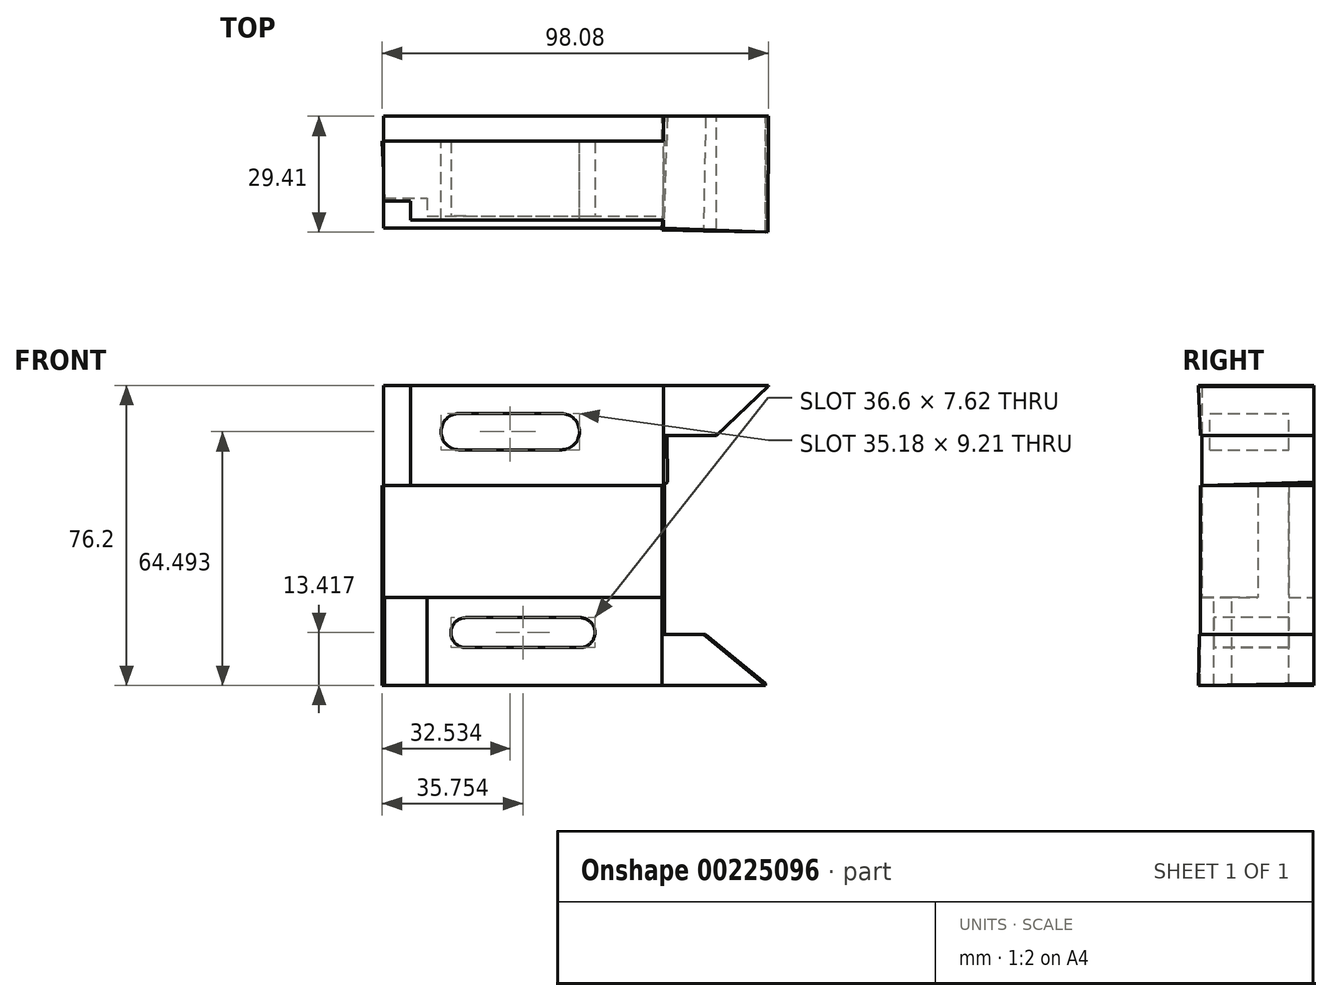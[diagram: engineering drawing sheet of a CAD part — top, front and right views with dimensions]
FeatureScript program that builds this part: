
annotation { "Feature Type Name" : "Feature", "Feature Type Description" : "" }
export const myFeature = defineFeature(function(context is Context, id is Id, definition is map)
    precondition{}
    {
        {
            var Q0;
            Q0=qCreatedBy(makeId("Front.planeOp"),FACE);
            var sketch = newSketch(context, id + "F0", { "sketchPlane" : qUnion([Q0])});
            skLineSegment(sketch, "E0.bottom", {"start": v(-31.28, 0) * mm, "end": v(39.84, 0) * mm});
            skLineSegment(sketch, "E0.top", {"start": v(-31.28, -28.45) * mm, "end": v(39.84, -28.45) * mm});
            skLineSegment(sketch, "E0.left", {"start": v(-31.28, 0) * mm, "end": v(-31.28, -28.45) * mm});
            skLineSegment(sketch, "E0.right", {"start": v(39.84, 0) * mm, "end": v(39.84, -28.45) * mm});
            skSolve(sketch);
        }
        {
            var Q0;
            Q0 = qSketchRegion(id + "F0", true);
            extrude(context, id + "F1", {"entities" : qUnion([Q0]), "depth" : 28.45 * mm});
        }
        {
            var Q0;
            Q0=makeQuery(id+"F1.opExtrude","SWEPT_FACE",FACE,{"disambiguationData":[OSD([sQuery(id+"F0.wireOp",EDGE,"E0.bottom")])]});
            var sketch = newSketch(context, id + "F2", { "sketchPlane" : qUnion([Q0])});
            skLineSegment(sketch, "E1", {"start": v(-31.28, -6.35) * mm, "end": v(39.84, -6.35) * mm});
            skLineSegment(sketch, "E2", {"start": v(39.84, -6.35) * mm, "end": v(39.84, 0) * mm});
            skLineSegment(sketch, "E3", {"start": v(39.84, 0) * mm, "end": v(39.84, 0) * mm});
            skLineSegment(sketch, "E4", {"start": v(39.84, -28.45) * mm, "end": v(39.84, -28.45) * mm});
            skLineSegment(sketch, "E5", {"start": v(39.84, -28.45) * mm, "end": v(39.84, -26.42) * mm});
            skLineSegment(sketch, "E6", {"start": v(39.84, -26.42) * mm, "end": v(-24.36, -26.42) * mm});
            skLineSegment(sketch, "E7", {"start": v(-24.36, -26.42) * mm, "end": v(-24.36, -21.59) * mm});
            skLineSegment(sketch, "E8", {"start": v(-24.36, -21.59) * mm, "end": v(-31.28, -21.59) * mm});
            skLineSegment(sketch, "E9", {"start": v(-31.28, -21.59) * mm, "end": v(-31.28, -6.35) * mm});
            skLineSegment(sketch, "E10", {"start": v(39.84, 0) * mm, "end": v(66.5, 0) * mm});
            skLineSegment(sketch, "E11", {"start": v(66.5, 0) * mm, "end": v(66.47, -29.37) * mm});
            skLineSegment(sketch, "E12", {"start": v(66.47, -29.37) * mm, "end": v(39.84, -28.45) * mm});
            skSolve(sketch);
        }
        {
            var Q0;
            {var subQ0=sQuery(id+"F2.wireOp",EDGE,"E1");Q0=makeQuery(id+"F2.imprint","IMPRINT",FACE,{"disambiguationData":[TD([[makeQuery(id+"F2.imprint","IMPRINT",EDGE,{"derivedFrom":subQ0}),-1.0]])]});}
            var Q1;
            {var subQ0=sQuery(id+"F2.wireOp",EDGE,"E2");Q1=makeQuery(id+"F2.imprint","IMPRINT",FACE,{"disambiguationData":[TD([[makeQuery(id+"F2.imprint","IMPRINT",EDGE,{"derivedFrom":subQ0}),-1.0]])]});}
            extrude(context, id + "F3", {"entities" : qUnion([Q0, Q1]), "operationType" : NewBodyOperationType.ADD, "oppositeDirection" : true, "depth" : 25.4 * mm});
        }
        {
            var Q0;
            Q0 = qSketchRegion(id + "F2", true);
            extrude(context, id + "F4", {"entities" : qUnion([Q0]), "operationType" : NewBodyOperationType.ADD, "depth" : 25.4 * mm});
        }
        {
            var Q0;
            Q0=qCreatedBy(makeId("Front.planeOp"),FACE);
            var sketch = newSketch(context, id + "F5", { "sketchPlane" : qUnion([Q0])});
            skLineSegment(sketch, "E13", {"start": v(-12.04, 18.3) * mm, "end": v(13.93, 18.3) * mm});
            skLineSegment(sketch, "E14", {"start": v(-12.04, 9.09) * mm, "end": v(13.93, 9.09) * mm});
            skArc(sketch, "E15", {"start": v(-12.04, 18.3) * mm, "mid": v(-16.64, 13.7) * mm, "end": v(-12.04, 9.09) * mm});
            skArc(sketch, "E16", {"start": v(13.93, 9.09) * mm, "mid": v(18.53, 13.7) * mm, "end": v(13.93, 18.3) * mm});
            skLineSegment(sketch, "E17", {"start": v(39.9, 0) * mm, "end": v(69.92, 0) * mm});
            skLineSegment(sketch, "E18", {"start": v(69.92, 0) * mm, "end": v(69.92, 28.45) * mm});
            skLineSegment(sketch, "E19", {"start": v(69.92, 28.45) * mm, "end": v(39.9, 0) * mm});
            skSolve(sketch);
        }
        {
            var Q0;
            Q0 = qSketchRegion(id + "F5", true);
            extrude(context, id + "F6", {"entities" : qUnion([Q0]), "operationType" : NewBodyOperationType.REMOVE, "endBound" : BoundingType.THROUGH_ALL, "depth" : 25.4 * mm});
        }
        {
            var Q0;
            {var subQ0=sQuery(id+"F2.wireOp",EDGE,"E12");Q0=makeQuery(id+"F4.boolean.opBoolean","MERGE",FACE,{"derivedFrom":[makeQuery(id+"F3.opExtrude","SWEPT_FACE",FACE,{"disambiguationData":[OSD([subQ0])]}),makeQuery(id+"F4.opExtrude","SWEPT_FACE",FACE,{"disambiguationData":[OSD([subQ0])]})]});}
            var sketch = newSketch(context, id + "F7", { "sketchPlane" : qUnion([Q0])});
            skPoint(sketch, "E20.0", {"position": v(40.8, 12.7) * mm});
            skLineSegment(sketch, "E21", {"start": v(40.8, 12.7) * mm, "end": v(54.27, 12.7) * mm});
            skLineSegment(sketch, "E22", {"start": v(54.27, 12.7) * mm, "end": v(40.85, 0) * mm});
            skLineSegment(sketch, "E23", {"start": v(40.85, 0) * mm, "end": v(40.8, 12.7) * mm});
            skSolve(sketch);
        }
        {
            var Q0;
            Q0 = qSketchRegion(id + "F7", true);
            extrude(context, id + "F8", {"entities" : qUnion([Q0]), "operationType" : NewBodyOperationType.REMOVE, "endBound" : BoundingType.THROUGH_ALL, "oppositeDirection" : true, "depth" : 25.4 * mm});
        }
        {
            var Q0;
            {var subQ2=sQuery(id+"F2.wireOp",EDGE,"E12");var subQ10=makeQuery(id+"F4.opExtrude","SWEPT_FACE",FACE,{"disambiguationData":[OSD([subQ2])]});var subQ11=sQuery(id+"F0.wireOp",EDGE,"E0.bottom");var subQ12=makeQuery(id+"F3.opExtrude","SWEPT_FACE",FACE,{"disambiguationData":[OSD([subQ2])]});Q0=makeQuery(id+"F8.boolean.opBoolean","SPLIT",FACE,{"disambiguationData":[TD([makeQuery(id+"F1.opExtrude","SWEPT_FACE",FACE,{"disambiguationData":[OSD([subQ11])]})])],"derivedFrom":makeQuery(id+"F4.boolean.opBoolean","MERGE",FACE,{"derivedFrom":[subQ12,subQ10]})});}
            var sketch = newSketch(context, id + "F9", { "sketchPlane" : qUnion([Q0])});
            skLineSegment(sketch, "E24.bottom", {"start": v(40.85, 0) * mm, "end": v(67.45, 0) * mm});
            skLineSegment(sketch, "E24.top", {"start": v(40.85, -25.4) * mm, "end": v(67.45, -25.4) * mm});
            skLineSegment(sketch, "E24.left", {"start": v(40.85, 0) * mm, "end": v(40.85, -25.4) * mm});
            skLineSegment(sketch, "E24.right", {"start": v(67.45, 0) * mm, "end": v(67.45, -25.4) * mm});
            skSolve(sketch);
        }
        {
            var Q0;
            Q0 = qSketchRegion(id + "F9", true);
            extrude(context, id + "F10", {"entities" : qUnion([Q0]), "operationType" : NewBodyOperationType.REMOVE, "endBound" : BoundingType.THROUGH_ALL, "oppositeDirection" : true, "depth" : 25.4 * mm});
        }
        {
            var Q0;
            Q0=qCreatedBy(makeId("Top.planeOp"),FACE);
            var sketch = newSketch(context, id + "F11", { "sketchPlane" : qUnion([Q0])});
            skLineSegment(sketch, "E25", {"start": v(-31.6, -6.35) * mm, "end": v(39.53, -6.35) * mm});
            skLineSegment(sketch, "E26", {"start": v(39.53, -6.35) * mm, "end": v(39.53, 0) * mm});
            skLineSegment(sketch, "E27", {"start": v(39.53, 0) * mm, "end": v(65.76, 0) * mm});
            skLineSegment(sketch, "E28", {"start": v(65.76, 0) * mm, "end": v(65.76, -29.4) * mm});
            skLineSegment(sketch, "E29", {"start": v(-31.03, -20.83) * mm, "end": v(-20.23, -20.83) * mm});
            skLineSegment(sketch, "E30", {"start": v(-20.23, -20.83) * mm, "end": v(-20.23, -25.37) * mm});
            skLineSegment(sketch, "E31", {"start": v(-20.23, -25.37) * mm, "end": v(33.45, -25.37) * mm});
            skLineSegment(sketch, "E32", {"start": v(33.45, -25.37) * mm, "end": v(39.53, -25.37) * mm});
            skLineSegment(sketch, "E33", {"start": v(39.53, -25.37) * mm, "end": v(39.53, -28.89) * mm});
            skLineSegment(sketch, "E34", {"start": v(65.76, -29.4) * mm, "end": v(39.53, -28.89) * mm});
            skLineSegment(sketch, "E35", {"start": v(-31.6, -6.35) * mm, "end": v(-31.03, -20.83) * mm});
            skSolve(sketch);
        }
        {
            var Q0;
            Q0 = qSketchRegion(id + "F11", true);
            extrude(context, id + "F12", {"entities" : qUnion([Q0]), "operationType" : NewBodyOperationType.ADD, "oppositeDirection" : true, "depth" : 50.8 * mm});
        }
        {
            var Q0;
            Q0=makeQuery(id+"F12.opExtrude","SWEPT_FACE",FACE,{"disambiguationData":[OSD([sQuery(id+"F11.wireOp",EDGE,"E31"),sQuery(id+"F11.wireOp",EDGE,"E32")])]});
            var sketch = newSketch(context, id + "F13", { "sketchPlane" : qUnion([Q0])});
            skLineSegment(sketch, "E36", {"start": v(-10.33, -33.57) * mm, "end": v(18.41, -33.57) * mm});
            skLineSegment(sketch, "E37", {"start": v(-10.33, -41.2) * mm, "end": v(18.41, -41.2) * mm});
            skArc(sketch, "E38", {"start": v(-10.33, -33.57) * mm, "mid": v(-14.14, -37.38) * mm, "end": v(-10.33, -41.2) * mm});
            skArc(sketch, "E39", {"start": v(18.41, -41.2) * mm, "mid": v(22.46, -37.38) * mm, "end": v(18.41, -33.57) * mm});
            skLineSegment(sketch, "E40", {"start": v(39.53, -28.45) * mm, "end": v(65.92, -50.14) * mm});
            skLineSegment(sketch, "E41", {"start": v(39.53, -28.45) * mm, "end": v(39.53, 0) * mm});
            skLineSegment(sketch, "E42", {"start": v(39.53, 0) * mm, "end": v(65.62, 0) * mm});
            skLineSegment(sketch, "E43", {"start": v(65.62, 0) * mm, "end": v(65.92, -50.14) * mm});
            skSolve(sketch);
        }
        {
            var Q0;
            Q0=makeQuery(id+"F13.imprint","IMPRINT",FACE,{"disambiguationData":[TD([[makeQuery(id+"F13.imprint","IMPRINT",EDGE,{"derivedFrom":sQuery(id+"F13.wireOp",EDGE,"E36")}),-1.0]])]});
            extrude(context, id + "F14", {"entities" : qUnion([Q0]), "operationType" : NewBodyOperationType.REMOVE, "endBound" : BoundingType.THROUGH_ALL, "oppositeDirection" : true, "depth" : 25.4 * mm});
        }
        {
            var Q0;
            Q0=makeQuery(id+"F12.opExtrude","SWEPT_FACE",FACE,{"disambiguationData":[OSD([sQuery(id+"F11.wireOp",EDGE,"E34")])]});
            var sketch = newSketch(context, id + "F15", { "sketchPlane" : qUnion([Q0])});
            skLineSegment(sketch, "E44", {"start": v(40.1, 0) * mm, "end": v(66.33, 0) * mm});
            skLineSegment(sketch, "E45", {"start": v(66.33, 0) * mm, "end": v(66.33, -50.8) * mm});
            skLineSegment(sketch, "E46", {"start": v(66.33, -50.8) * mm, "end": v(40.1, -29.18) * mm});
            skLineSegment(sketch, "E47", {"start": v(40.1, -29.18) * mm, "end": v(40.1, 0) * mm});
            skSolve(sketch);
        }
        {
            var Q0;
            Q0 = qSketchRegion(id + "F15", true);
            extrude(context, id + "F16", {"entities" : qUnion([Q0]), "operationType" : NewBodyOperationType.REMOVE, "endBound" : BoundingType.THROUGH_ALL, "oppositeDirection" : true, "depth" : 25.4 * mm});
        }
        {
            var Q0;
            Q0=makeQuery(id+"F12.opExtrude","SWEPT_FACE",FACE,{"disambiguationData":[OSD([sQuery(id+"F11.wireOp",EDGE,"E34")])]});
            var sketch = newSketch(context, id + "F17", { "sketchPlane" : qUnion([Q0])});
            skLineSegment(sketch, "E48", {"start": v(40.1, -29.18) * mm, "end": v(50.58, -37.82) * mm});
            skLineSegment(sketch, "E49", {"start": v(50.58, -37.82) * mm, "end": v(40.1, -37.82) * mm});
            skLineSegment(sketch, "E50", {"start": v(40.1, -37.82) * mm, "end": v(40.1, -29.18) * mm});
            skSolve(sketch);
        }
        {
            var Q0;
            Q0 = qSketchRegion(id + "F17", true);
            extrude(context, id + "F18", {"entities" : qUnion([Q0]), "operationType" : NewBodyOperationType.REMOVE, "endBound" : BoundingType.THROUGH_ALL, "oppositeDirection" : true, "depth" : 25.4 * mm});
        }
    });
